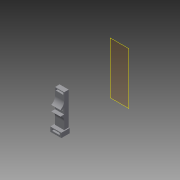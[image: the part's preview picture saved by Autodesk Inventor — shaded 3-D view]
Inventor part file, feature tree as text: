
AUTODESK INVENTOR PART (.ipt)
format: ipt  version: 2015 (Build 190159000, 159)  size: 106,496 bytes
history: native  units: in
note: dims shown in document units (in); Inventor stores cm internally (conversion verified against a paired STEP export)
features: other x3, plane x1
ambient origin geometry x8: Origin, YZ Plane, XZ Plane, XY Plane, X Axis, Y Axis, Z Axis, Center Point
bodies: Solid1 (feature_tree)
feature tree (4):
  other  "side piece.ipt"
  other  "Solid1::side piece.ipt"
  other  "TaggingFeature1"
  plane  "Work Plane1"
